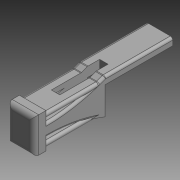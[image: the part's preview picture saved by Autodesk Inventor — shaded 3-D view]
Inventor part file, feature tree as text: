
AUTODESK INVENTOR PART (.ipt)
format: ipt  version: 2018 (Build 220112000, 112)  size: 241,664 bytes
history: native  units: mm
features: extrude x7, sketch x7, projected_geometry x3, fillet x2, chamfer x2, other x1
ambient origin geometry x8: Origin, YZ Plane, XZ Plane, XY Plane, X Axis, Y Axis, Z Axis, Center Point
bodies: Body1 (feature_tree)
feature tree (22):
  other  "ソリッド1"
  extrude  "押し出し1"  Depth=14.5mm
  extrude  "押し出し2"  Depth=11.0mm
  extrude  "押し出し4"  Depth=37.5mm TaperAngle=0.0deg
  extrude  "押し出し6"  Depth=33.0mm
  extrude  "押し出し7"  Depth=10.5mm
  fillet  "フィレット1"  Radius=37.5mm
  chamfer  "面取り2"  Distance=25.0mm
  extrude  "押し出し8"  Depth=3.5mm
  fillet  "フィレット2"  Radius=3.5mm
  extrude  "押し出し9"  Depth=5.0mm
  chamfer  "面取り3"  Distance=25.0mm
  sketch  "スケッチ1"
  sketch  "スケッチ2"
  sketch  "スケッチ4"
  projected_geometry  "投影ループ1"
  sketch  "スケッチ5"
  sketch  "スケッチ6"
  sketch  "スケッチ8"
  projected_geometry  "投影ループ2"
  sketch  "スケッチ9"
  projected_geometry  "投影ループ3"
